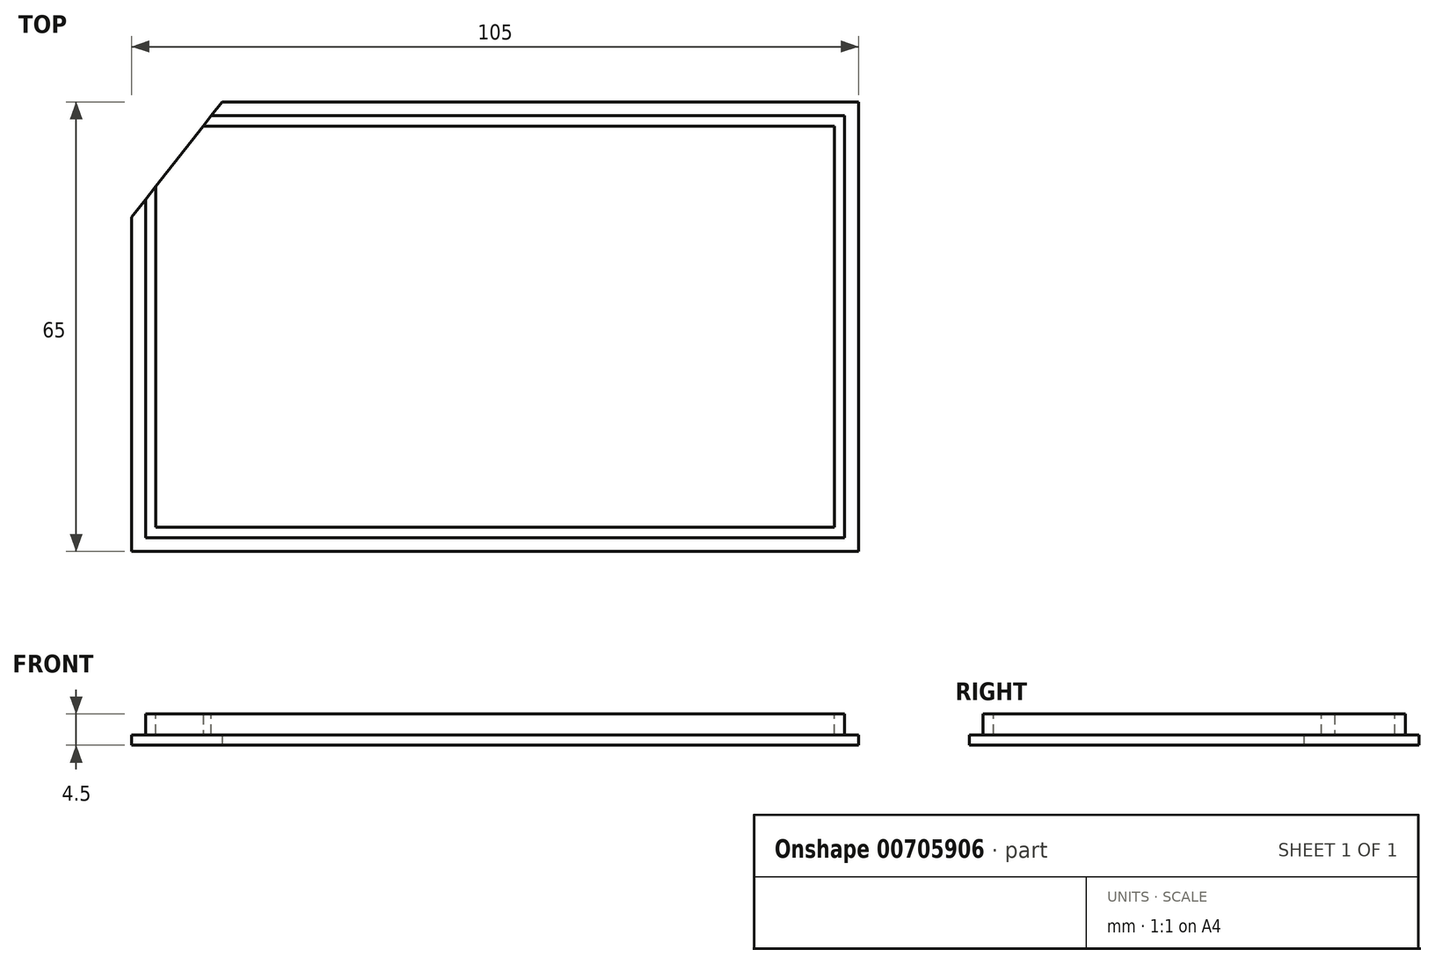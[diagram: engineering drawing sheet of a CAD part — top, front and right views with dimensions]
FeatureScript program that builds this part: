
annotation { "Feature Type Name" : "Feature", "Feature Type Description" : "" }
export const myFeature = defineFeature(function(context is Context, id is Id, definition is map)
    precondition{}
    {
        {
            var Q0;
            Q0=qCreatedBy(makeId("Top.planeOp"),FACE);
            var sketch = newSketch(context, id + "F0", { "sketchPlane" : qUnion([Q0])});
            skLineSegment(sketch, "E0.bottom", {"start": v(52.5, -32.5) * mm, "end": v(-52.5, -32.5) * mm});
            skLineSegment(sketch, "E0.top", {"start": v(52.5, 32.5) * mm, "end": v(-52.5, 32.5) * mm});
            skLineSegment(sketch, "E0.left", {"start": v(52.5, -32.5) * mm, "end": v(52.5, 32.5) * mm});
            skLineSegment(sketch, "E0.right", {"start": v(-52.5, -32.5) * mm, "end": v(-52.5, 32.5) * mm});
            skPoint(sketch, "E0.middle", {"position": v(0, 0) * mm});
            skLineSegment(sketch, "E1", {"start": v(-39.43, 32.5) * mm, "end": v(-52.5, 15.86) * mm});
            skSolve(sketch);
        }
        {
            var Q0;
            Q0 = qSketchRegion(id + "F0", true);
            extrude(context, id + "F1", {"entities" : qUnion([Q0]), "depth" : 1.5 * mm, "offsetDistance" : 25 * mm});
        }
        {
            var Q0;
            Q0=makeQuery(id+"F1.opExtrude","CAP_FACE",FACE,{"disambiguationData":[OSD([sQuery(id+"F0.wireOp",EDGE,"E0.bottom"),sQuery(id+"F0.wireOp",EDGE,"E0.top"),sQuery(id+"F0.wireOp",EDGE,"E0.left"),sQuery(id+"F0.wireOp",EDGE,"E0.right")])],"isStart":false});
            var sketch = newSketch(context, id + "F2", { "sketchPlane" : qUnion([Q0])});
            skLineSegment(sketch, "E2.bottom", {"start": v(50.5, -30.5) * mm, "end": v(-50.5, -30.5) * mm});
            skLineSegment(sketch, "E2.top", {"start": v(50.5, 30.5) * mm, "end": v(-50.5, 30.5) * mm});
            skLineSegment(sketch, "E2.left", {"start": v(50.5, -30.5) * mm, "end": v(50.5, 30.5) * mm});
            skLineSegment(sketch, "E2.right", {"start": v(-50.5, -30.5) * mm, "end": v(-50.5, 30.5) * mm});
            skPoint(sketch, "E2.middle", {"position": v(0, 0) * mm});
            skSolve(sketch);
        }
        {
            var Q0;
            Q0 = qSketchRegion(id + "F2", true);
            extrude(context, id + "F3", {"entities" : qUnion([Q0]), "operationType" : NewBodyOperationType.ADD, "depth" : 3 * mm, "offsetDistance" : 25 * mm});
        }
        {
            var Q0;
            Q0=makeQuery(id+"F3.opExtrude","CAP_FACE",FACE,{"disambiguationData":[OSD([sQuery(id+"F2.wireOp",EDGE,"E2.bottom"),sQuery(id+"F2.wireOp",EDGE,"E2.top"),sQuery(id+"F2.wireOp",EDGE,"E2.left"),sQuery(id+"F2.wireOp",EDGE,"E2.right")])],"isStart":false});
            var sketch = newSketch(context, id + "F4", { "sketchPlane" : qUnion([Q0])});
            skLineSegment(sketch, "E3.bottom", {"start": v(49, -29) * mm, "end": v(-49, -29) * mm});
            skLineSegment(sketch, "E3.top", {"start": v(49, 29) * mm, "end": v(-49, 29) * mm});
            skLineSegment(sketch, "E3.left", {"start": v(49, -29) * mm, "end": v(49, 29) * mm});
            skLineSegment(sketch, "E3.right", {"start": v(-49, -29) * mm, "end": v(-49, 29) * mm});
            skPoint(sketch, "E3.middle", {"position": v(0, 0) * mm});
            skSolve(sketch);
        }
        {
            var Q0;
            Q0 = qSketchRegion(id + "F4", true);
            extrude(context, id + "F5", {"entities" : qUnion([Q0]), "operationType" : NewBodyOperationType.REMOVE, "oppositeDirection" : true, "depth" : 3 * mm, "offsetDistance" : 25 * mm});
        }
        {
            var Q0;
            {var subQ3=sQuery(id+"F0.wireOp",EDGE,"E1");Q0=makeQuery(id+"F0.imprint","IMPRINT",FACE,{"disambiguationData":[TD([[makeQuery(id+"F0.imprint","IMPRINT",EDGE,{"derivedFrom":subQ3}),-1.0]])]});}
            extrude(context, id + "F6", {"entities" : qUnion([Q0]), "operationType" : NewBodyOperationType.REMOVE, "depth" : 25 * mm, "offsetDistance" : 25 * mm});
        }
    });
